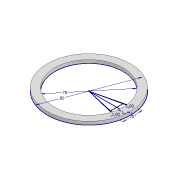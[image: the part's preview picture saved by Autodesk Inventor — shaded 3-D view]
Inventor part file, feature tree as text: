
AUTODESK INVENTOR PART (.ipt)
format: ipt  version: 2020.3 (Build 243373000, 373)  size: 100,864 bytes
history: native  units: mm
features: extrude x2, sketch x1
ambient origin geometry x8: Origin, YZ Plane, XZ Plane, XY Plane, X Axis, Y Axis, Z Axis, Center Point
bodies: Solid1 (feature_tree)
feature tree (3):
  sketch  "Sketch1"  dims[d0=85.0mm d1=70.0mm d2=20.0mm d4=1.0mm d5=1.0mm d6=0.174533mm d7=0.174533mm d8=3.2mm d9=0.0mm d10=2.5mm d11=0.0mm]
  extrude  "Extrusion1"  Depth=2.5mm
  extrude  "Extrusion2"  Depth=2.5mm
